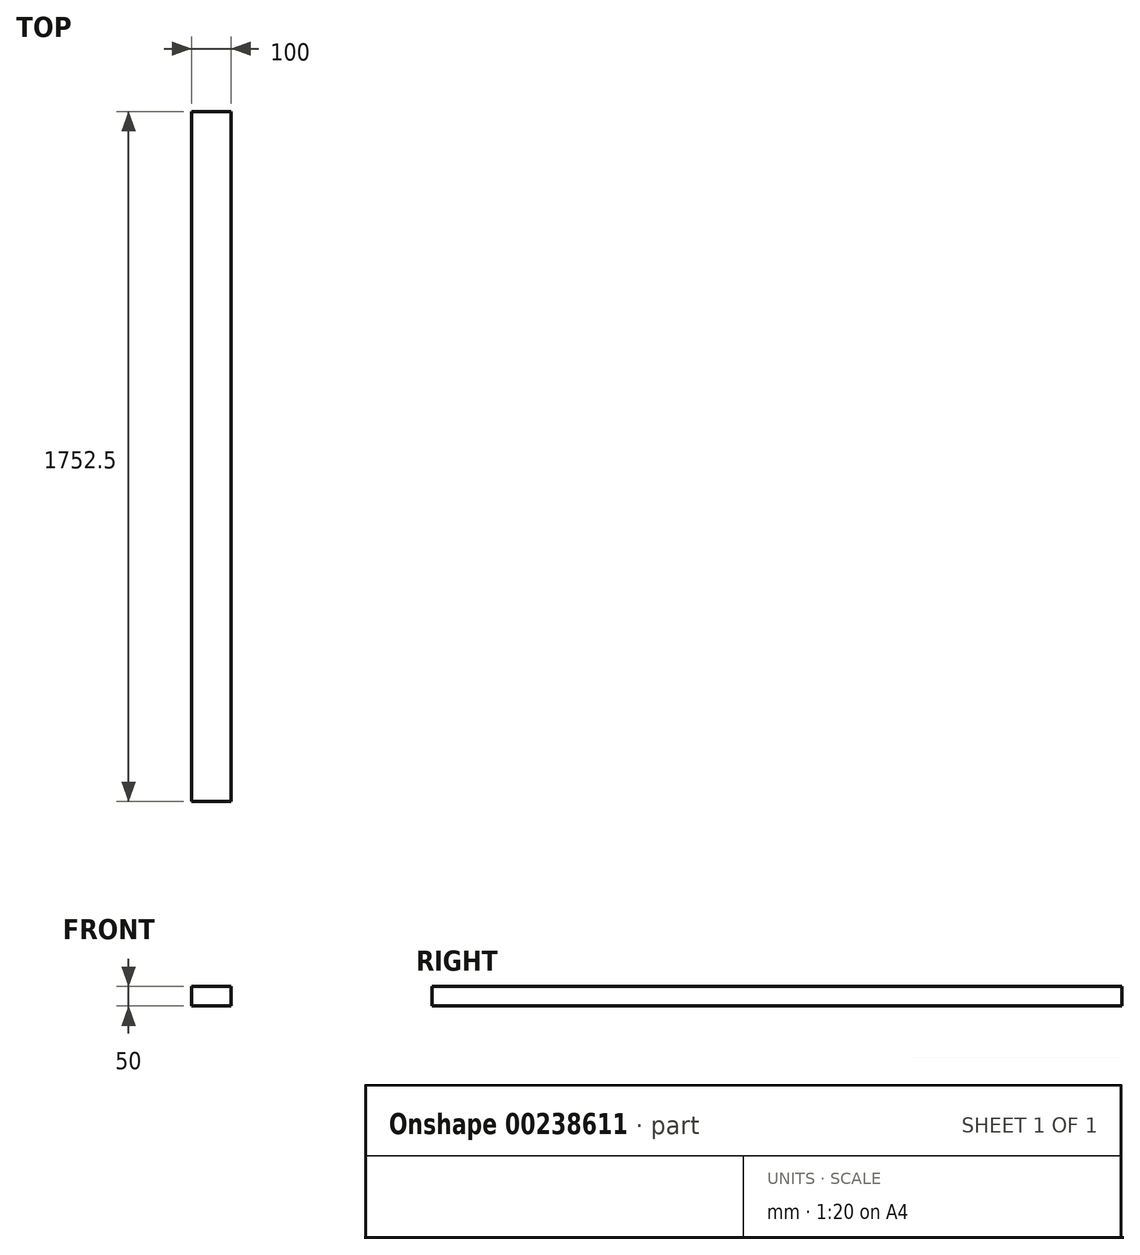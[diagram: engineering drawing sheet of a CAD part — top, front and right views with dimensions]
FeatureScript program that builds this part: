
annotation { "Feature Type Name" : "Feature", "Feature Type Description" : "" }
export const myFeature = defineFeature(function(context is Context, id is Id, definition is map)
    precondition{}
    {
        {
            var Q0;
            Q0=qCreatedBy(makeId("Front.planeOp"),FACE);
            var sketch = newSketch(context, id + "F0", { "sketchPlane" : qUnion([Q0])});
            skLineSegment(sketch, "E0.bottom", {"start": v(50, -25) * mm, "end": v(-50, -25) * mm});
            skLineSegment(sketch, "E0.top", {"start": v(50, 25) * mm, "end": v(-50, 25) * mm});
            skLineSegment(sketch, "E0.left", {"start": v(50, -25) * mm, "end": v(50, 25) * mm});
            skLineSegment(sketch, "E0.right", {"start": v(-50, -25) * mm, "end": v(-50, 25) * mm});
            skPoint(sketch, "E0.middle", {"position": v(0, 0) * mm});
            skSolve(sketch);
        }
        {
            var Q0;
            Q0=makeQuery(id+"F0.imprint","IMPRINT",FACE,{"disambiguationData":[TD([[makeQuery(id+"F0.imprint","IMPRINT",EDGE,{"derivedFrom":sQuery(id+"F0.wireOp",EDGE,"E0.bottom")}),-1.0]])]});
            extrude(context, id + "F1", {"entities" : qUnion([Q0]), "depth" : (1822.5 - 70) * mm});
        }
    });
